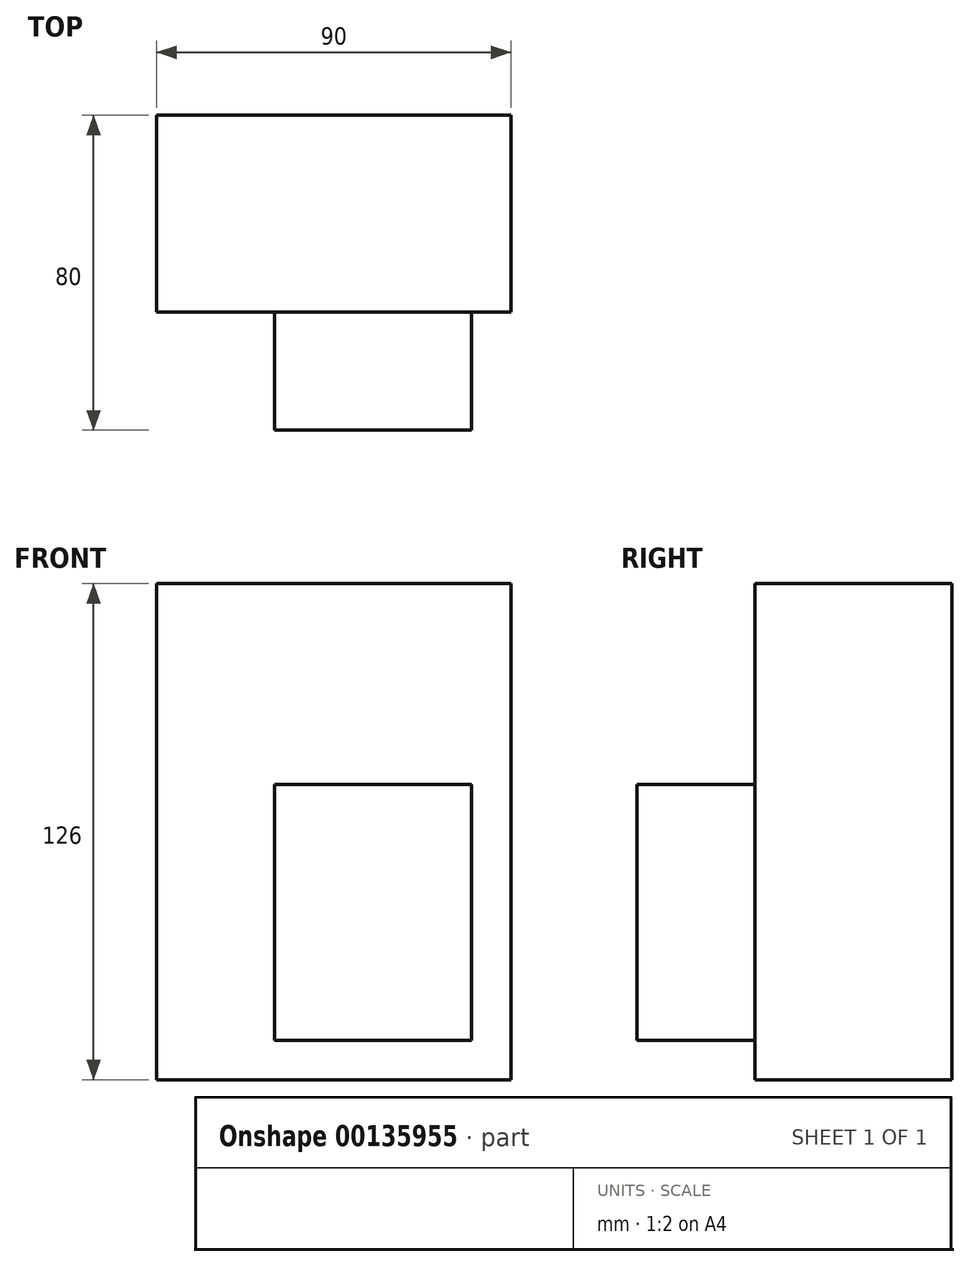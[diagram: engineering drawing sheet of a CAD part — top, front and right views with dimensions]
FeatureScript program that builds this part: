
annotation { "Feature Type Name" : "Feature", "Feature Type Description" : "" }
export const myFeature = defineFeature(function(context is Context, id is Id, definition is map)
    precondition{}
    {
        {
            var Q0;
            Q0=qCreatedBy(makeId("Front.planeOp"),FACE);
            var sketch = newSketch(context, id + "F0", { "sketchPlane" : qUnion([Q0])});
            skLineSegment(sketch, "E0.bottom", {"start": v(45, -63) * mm, "end": v(-45, -63) * mm});
            skLineSegment(sketch, "E0.top", {"start": v(45, 63) * mm, "end": v(-45, 63) * mm});
            skLineSegment(sketch, "E0.left", {"start": v(45, -63) * mm, "end": v(45, 63) * mm});
            skLineSegment(sketch, "E0.right", {"start": v(-45, -63) * mm, "end": v(-45, 63) * mm});
            skPoint(sketch, "E0.middle", {"position": v(0, 0) * mm});
            skSolve(sketch);
        }
        {
            var Q0;
            Q0 = qSketchRegion(id + "F0", true);
            extrude(context, id + "F1", {"entities" : qUnion([Q0]), "endBound" : BoundingType.SYMMETRIC, "depth" : 50 * mm});
        }
        {
            var Q0;
            Q0=makeQuery(id+"F1.opExtrude","CAP_FACE",FACE,{"disambiguationData":[OSD([sQuery(id+"F0.wireOp",EDGE,"E0.bottom"),sQuery(id+"F0.wireOp",EDGE,"E0.top"),sQuery(id+"F0.wireOp",EDGE,"E0.left"),sQuery(id+"F0.wireOp",EDGE,"E0.right")])],"isStart":false});
            var sketch = newSketch(context, id + "F2", { "sketchPlane" : qUnion([Q0])});
            skLineSegment(sketch, "E1.bottom", {"start": v(-15, 12) * mm, "end": v(35, 12) * mm});
            skLineSegment(sketch, "E1.top", {"start": v(-15, -53) * mm, "end": v(35, -53) * mm});
            skLineSegment(sketch, "E1.left", {"start": v(-15, 12) * mm, "end": v(-15, -53) * mm});
            skLineSegment(sketch, "E1.right", {"start": v(35, 12) * mm, "end": v(35, -53) * mm});
            skSolve(sketch);
        }
        {
            var Q0;
            Q0 = qSketchRegion(id + "F2", true);
            extrude(context, id + "F3", {"entities" : qUnion([Q0]), "operationType" : NewBodyOperationType.ADD, "depth" : 30 * mm});
        }
    });
